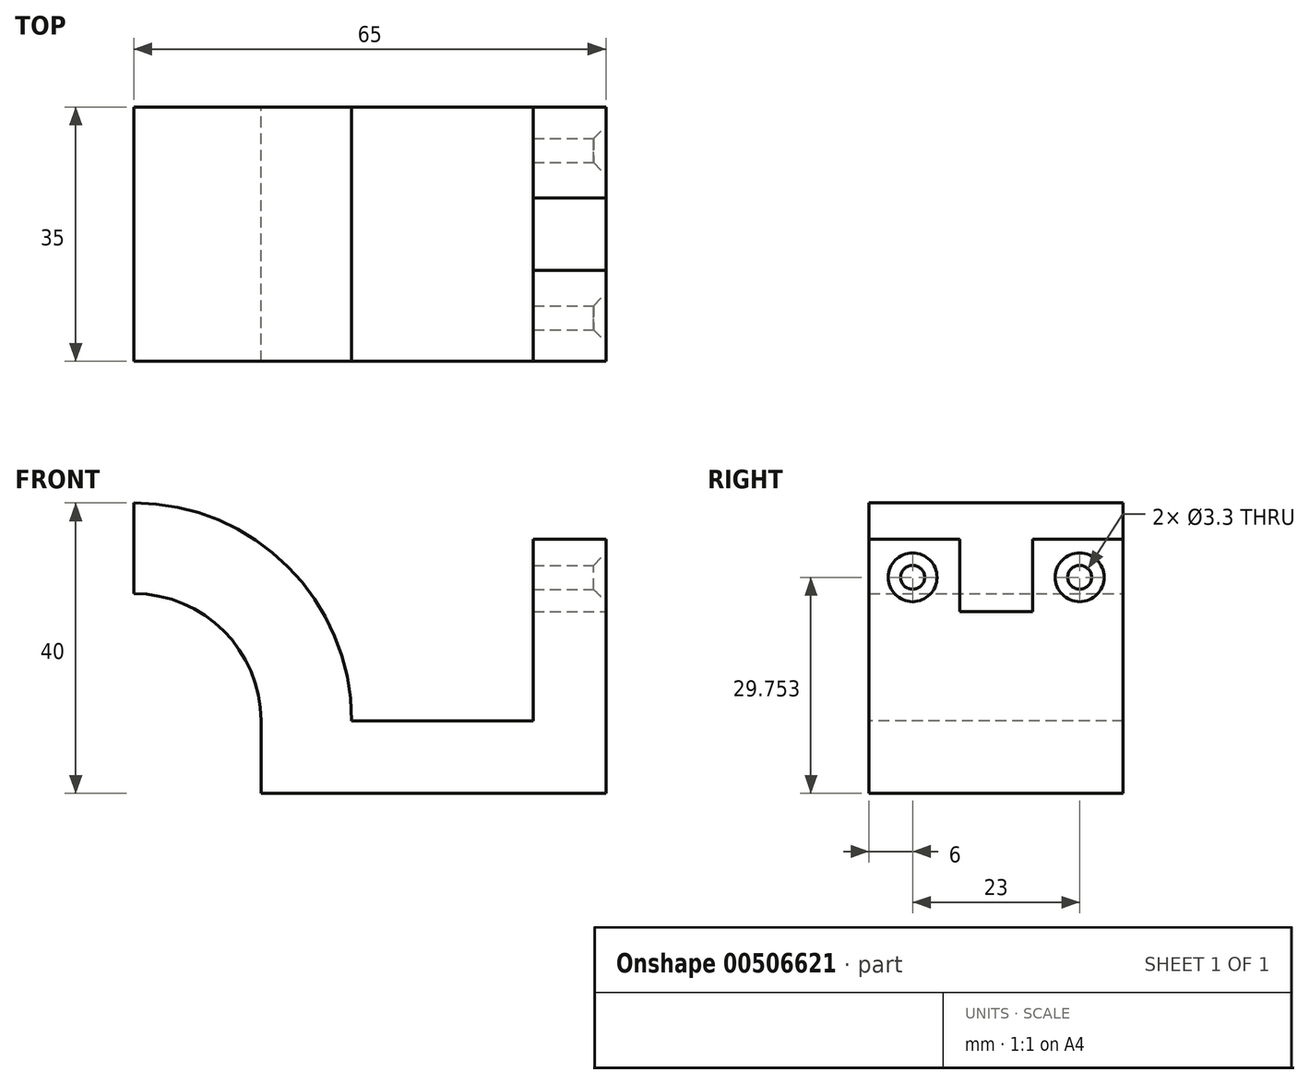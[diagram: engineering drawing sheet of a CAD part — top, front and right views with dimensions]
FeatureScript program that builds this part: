
annotation { "Feature Type Name" : "Feature", "Feature Type Description" : "" }
export const myFeature = defineFeature(function(context is Context, id is Id, definition is map)
    precondition{}
    {
        {
            var Q0;
            Q0=qCreatedBy(makeId("Front.planeOp"),FACE);
            var sketch = newSketch(context, id + "F0", { "sketchPlane" : qUnion([Q0])});
            skLineSegment(sketch, "E0.bottom", {"start": v(0, 0) * mm, "end": v(-80, 0) * mm});
            skLineSegment(sketch, "E0.top", {"start": v(0, 10) * mm, "end": v(-80, 10) * mm});
            skLineSegment(sketch, "E0.left", {"start": v(0, 0) * mm, "end": v(0, 10) * mm});
            skLineSegment(sketch, "E0.right", {"start": v(-80, 0) * mm, "end": v(-80, 10) * mm});
            skCircle(sketch, "E1", {"center": v(-65, 10) * mm, "radius": 17.5 * mm});
            skCircle(sketch, "E2", {"center": v(-65, 10) * mm, "radius": 30 * mm});
            skLineSegment(sketch, "E3", {"start": v(-47.5, 10) * mm, "end": v(-47.5, 0) * mm});
            skLineSegment(sketch, "E4", {"start": v(-65, 10) * mm, "end": v(-65, 40) * mm});
            skSolve(sketch);
        }
        {
            var Q0;
            {var subQ0=sQuery(id+"F0.wireOp",EDGE,"E0.left");Q0=makeQuery(id+"F0.imprint","IMPRINT",FACE,{"disambiguationData":[TD([[makeQuery(id+"F0.imprint","IMPRINT",EDGE,{"derivedFrom":subQ0}),1.0]])]});}
            var Q1;
            {var subQ0=sQuery(id+"F0.wireOp",EDGE,"E3");Q1=makeQuery(id+"F0.imprint","IMPRINT",FACE,{"disambiguationData":[TD([[makeQuery(id+"F0.imprint","IMPRINT",EDGE,{"derivedFrom":subQ0}),1.0]])]});}
            var Q2;
            {var subQ3=sQuery(id+"F0.wireOp",EDGE,"E2");var subQ5=sQuery(id+"F0.wireOp",EDGE,"E4");var subQ7=makeQuery(id+"F0.imprint","INTERSECT",VERTEX,{"derivedFrom":[subQ3,subQ5]});Q2=makeQuery(id+"F0.imprint","IMPRINT",FACE,{"disambiguationData":[TD([[makeQuery(id+"F0.imprint","IMPRINT",EDGE,{"disambiguationData":[TD([[subQ7,1.0]])],"derivedFrom":subQ3}),1.0]])]});}
            extrude(context, id + "F1", {"entities" : qUnion([Q0, Q1, Q2]), "depth" : 35 * mm});
        }
        {
            var Q0;
            Q0=qCreatedBy(makeId("Right.planeOp"),FACE);
            var sketch = newSketch(context, id + "F2", { "sketchPlane" : qUnion([Q0])});
            skLineSegment(sketch, "E5.bottom", {"start": v(0, 0) * mm, "end": v(-35, 0) * mm});
            skLineSegment(sketch, "E5.top", {"start": v(0, 35) * mm, "end": v(-35, 35) * mm});
            skLineSegment(sketch, "E5.left", {"start": v(0, 0) * mm, "end": v(0, 35) * mm});
            skLineSegment(sketch, "E5.right", {"start": v(-35, 0) * mm, "end": v(-35, 35) * mm});
            skLineSegment(sketch, "E6.bottom", {"start": v(-12.5, 25) * mm, "end": v(-22.5, 25) * mm});
            skLineSegment(sketch, "E6.top", {"start": v(-12.5, 45) * mm, "end": v(-22.5, 45) * mm});
            skLineSegment(sketch, "E6.left", {"start": v(-12.5, 25) * mm, "end": v(-12.5, 45) * mm});
            skLineSegment(sketch, "E6.right", {"start": v(-22.5, 25) * mm, "end": v(-22.5, 45) * mm});
            skPoint(sketch, "E6.middle", {"position": v(-17.5, 35) * mm});
            skPoint(sketch, "E7", {"position": v(-29, 29.75) * mm});
            skPoint(sketch, "E8", {"position": v(-6, 29.75) * mm});
            skSolve(sketch);
        }
        {
            var Q0;
            Q0=makeQuery(id+"F2.imprint","IMPRINT",FACE,{"disambiguationData":[TD([[makeQuery(id+"F2.imprint","IMPRINT",EDGE,{"derivedFrom":sQuery(id+"F2.wireOp",EDGE,"E5.bottom")}),-1.0]])]});
            extrude(context, id + "F3", {"entities" : qUnion([Q0]), "operationType" : NewBodyOperationType.ADD, "oppositeDirection" : true, "depth" : 10 * mm});
        }
        {
            var Q0;
            Q0=sQuery(id+"F2.wireOp",VERTEX,"E7");
            var Q1;
            Q1=sQuery(id+"F2.wireOp",VERTEX,"E8");
            var Q2;
            Q2=makeQuery(id+"F1.opExtrude","SWEPT_BODY",BODY,{"disambiguationData":[OSD([sQuery(id+"F0.wireOp",EDGE,"E0.bottom"),sQuery(id+"F0.wireOp",EDGE,"E0.top"),sQuery(id+"F0.wireOp",EDGE,"E0.left"),sQuery(id+"F0.wireOp",EDGE,"E1"),sQuery(id+"F0.wireOp",EDGE,"E2"),sQuery(id+"F0.wireOp",EDGE,"E3"),sQuery(id+"F0.wireOp",EDGE,"E4")])]});
            hole(context, id + "F4", {"style" : HoleStyle.C_SINK, "endStyle" : HoleEndStyle.BLIND, "standardTappedOrClearance" : lookupTablePath({ "standard" : "ISO", "fit" : "Normal", "size" : "M3", "type" : "Clearance" }), "standardBlindInLast" : lookupTablePath({ "fit" : "Standard", "standard" : "ISO", "size" : "M3", "type" : "Clearance" }), "holeDiameter" : 3.3 * mm, "cSinkDiameter" : 6.72 * mm, "cSinkAngle" : 90 * degree, "holeDepth" : 13.5 * mm, "isTappedThrough" : true, "tappedDepth" : 12 * mm, "tapClearance" : 3, "locations" : qUnion([Q0, Q1]), "scope" : qUnion([Q2])});
        }
    });
